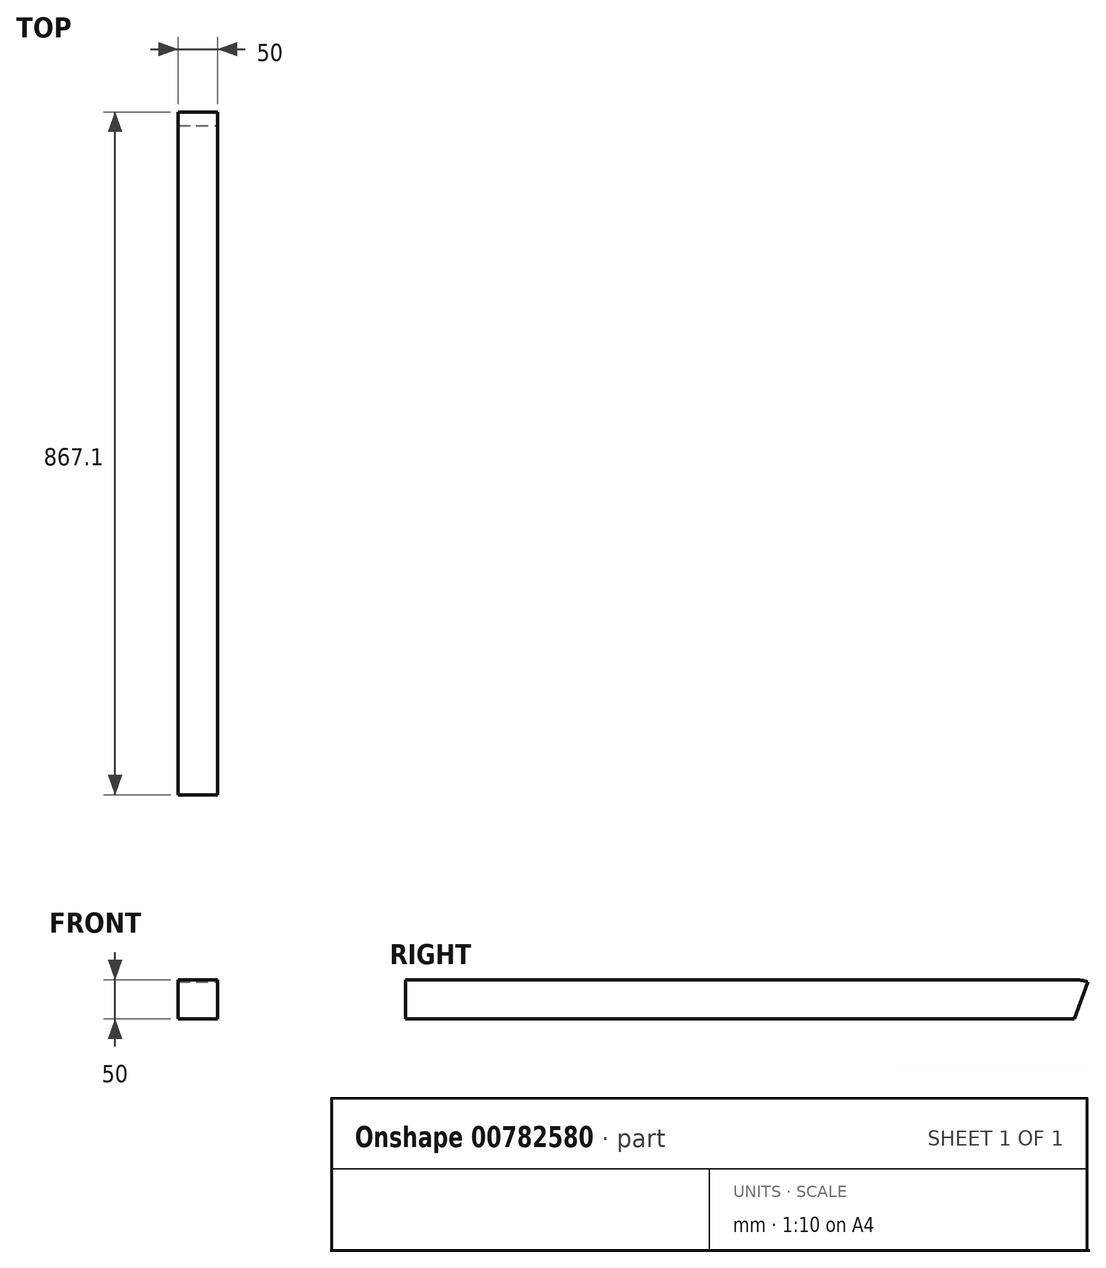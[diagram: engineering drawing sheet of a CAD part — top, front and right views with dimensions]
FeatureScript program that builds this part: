
annotation { "Feature Type Name" : "Feature", "Feature Type Description" : "" }
export const myFeature = defineFeature(function(context is Context, id is Id, definition is map)
    precondition{}
    {
        {
            var Q0;
            Q0=qCreatedBy(makeId("Front.planeOp"),FACE);
            var sketch = newSketch(context, id + "F0", { "sketchPlane" : qUnion([Q0])});
            skLineSegment(sketch, "E0.bottom", {"start": v(0, 0) * mm, "end": v(50, 0) * mm});
            skLineSegment(sketch, "E0.top", {"start": v(0, 50) * mm, "end": v(50, 50) * mm});
            skLineSegment(sketch, "E0.left", {"start": v(0, 0) * mm, "end": v(0, 50) * mm});
            skLineSegment(sketch, "E0.right", {"start": v(50, 0) * mm, "end": v(50, 50) * mm});
            skSolve(sketch);
        }
        {
            var Q0;
            Q0 = qSketchRegion(id + "F0", true);
            extrude(context, id + "F1", {"entities" : qUnion([Q0]), "depth" : 850 * mm, "offsetDistance" : 25 * mm});
        }
        {
            var Q0;
            Q0=qCreatedBy(makeId("Front.planeOp"),FACE);
            var sketch = newSketch(context, id + "F2", { "sketchPlane" : qUnion([Q0])});
            skLineSegment(sketch, "E1.bottom", {"start": v(0, 0) * mm, "end": v(50, 0) * mm});
            skLineSegment(sketch, "E1.top", {"start": v(0, 50) * mm, "end": v(50, 50) * mm});
            skLineSegment(sketch, "E1.left", {"start": v(0, 0) * mm, "end": v(0, 50) * mm});
            skLineSegment(sketch, "E1.right", {"start": v(50, 0) * mm, "end": v(50, 50) * mm});
            skSolve(sketch);
        }
        {
            var Q0;
            Q0=makeQuery(id+"F2.imprint","IMPRINT",FACE,{"disambiguationData":[TD([[makeQuery(id+"F2.imprint","IMPRINT",EDGE,{"derivedFrom":sQuery(id+"F2.wireOp",EDGE,"E1.bottom")}),1.0]])]});
            var Q1;
            Q1=sQuery(id+"F2.wireOp",EDGE,"E1.bottom");
            revolve(context, id + "F3", {"operationType" : NewBodyOperationType.ADD, "surfaceOperationType" : NewSurfaceOperationType.NEW, "entities" : qUnion([Q0]), "axis" : qUnion([Q1]), "revolveType" : RevolveType.ONE_DIRECTION, "oppositeDirection" : true, "angle" : 20 * degree});
        }
    });
